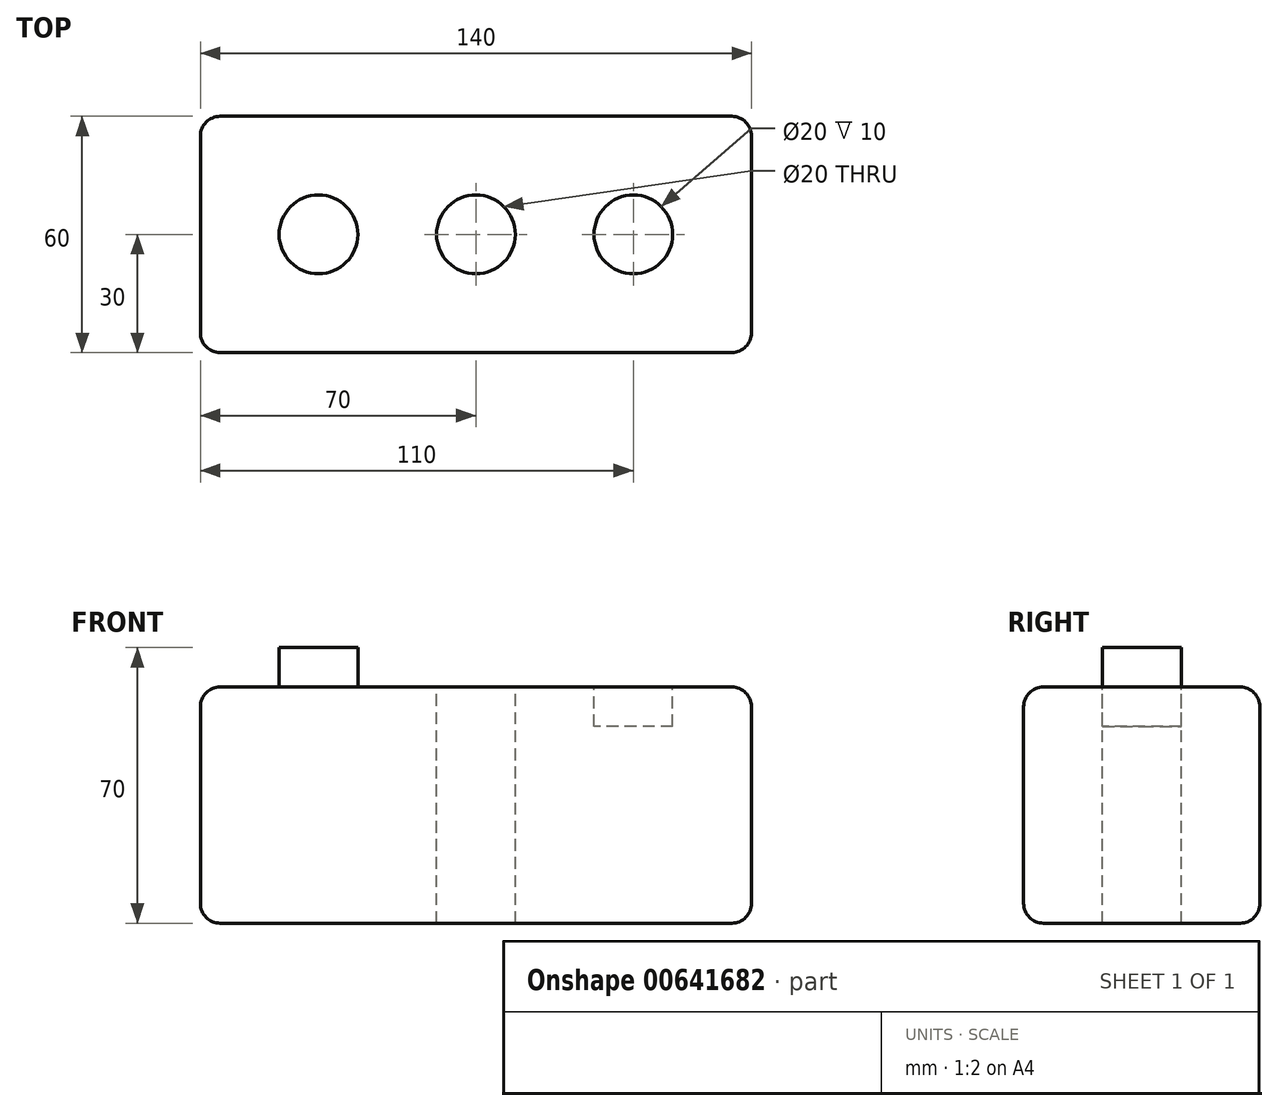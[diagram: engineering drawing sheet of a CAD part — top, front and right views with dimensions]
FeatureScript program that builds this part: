
annotation { "Feature Type Name" : "Feature", "Feature Type Description" : "" }
export const myFeature = defineFeature(function(context is Context, id is Id, definition is map)
    precondition{}
    {
        {
            var Q0;
            Q0=qCreatedBy(makeId("Top.planeOp"),FACE);
            var sketch = newSketch(context, id + "F0", { "sketchPlane" : qUnion([Q0])});
            skLineSegment(sketch, "E0.bottom", {"start": v(-70, 30) * mm, "end": v(70, 30) * mm});
            skLineSegment(sketch, "E0.top", {"start": v(-70, -30) * mm, "end": v(70, -30) * mm});
            skLineSegment(sketch, "E0.left", {"start": v(-70, 30) * mm, "end": v(-70, -30) * mm});
            skLineSegment(sketch, "E0.right", {"start": v(70, 30) * mm, "end": v(70, -30) * mm});
            skPoint(sketch, "E0.middle", {"position": v(0, 0) * mm});
            skSolve(sketch);
        }
        {
            var Q0;
            Q0 = qSketchRegion(id + "F0", true);
            extrude(context, id + "F1", {"entities" : qUnion([Q0]), "depth" : 60 * mm, "offsetDistance" : 25 * mm});
        }
        {
            var Q0;
            Q0=makeQuery(id+"F1.opExtrude","CAP_FACE",FACE,{"disambiguationData":[OSD([sQuery(id+"F0.wireOp",EDGE,"E0.bottom"),sQuery(id+"F0.wireOp",EDGE,"E0.top"),sQuery(id+"F0.wireOp",EDGE,"E0.left"),sQuery(id+"F0.wireOp",EDGE,"E0.right")])],"isStart":false});
            var sketch = newSketch(context, id + "F2", { "sketchPlane" : qUnion([Q0])});
            skCircle(sketch, "E1", {"center": v(-40, 0) * mm, "radius": 10 * mm});
            skSolve(sketch);
        }
        {
            var Q0;
            Q0=makeQuery(id+"F2.imprint","IMPRINT",FACE,{"disambiguationData":[TD([[makeQuery(id+"F2.imprint","IMPRINT",EDGE,{"derivedFrom":sQuery(id+"F2.wireOp",EDGE,"E1")}),-1.0]])]});
            var sketch = newSketch(context, id + "F3", { "sketchPlane" : qUnion([Q0])});
            skCircle(sketch, "E2", {"center": v(40, 0) * mm, "radius": 10 * mm});
            skSolve(sketch);
        }
        {
            var Q0;
            Q0=makeQuery(id+"F2.imprint","IMPRINT",FACE,{"disambiguationData":[TD([[makeQuery(id+"F2.imprint","IMPRINT",EDGE,{"derivedFrom":sQuery(id+"F2.wireOp",EDGE,"E1")}),-1.0]])]});
            var sketch = newSketch(context, id + "F4", { "sketchPlane" : qUnion([Q0])});
            skCircle(sketch, "E3", {"center": v(0, 0) * mm, "radius": 10 * mm});
            skSolve(sketch);
        }
        {
            var Q0;
            Q0 = qSketchRegion(id + "F2", true);
            extrude(context, id + "F5", {"entities" : qUnion([Q0]), "operationType" : NewBodyOperationType.ADD, "depth" : 10 * mm, "offsetDistance" : 25 * mm});
        }
        {
            var Q0;
            Q0 = qSketchRegion(id + "F3", true);
            extrude(context, id + "F6", {"entities" : qUnion([Q0]), "operationType" : NewBodyOperationType.REMOVE, "oppositeDirection" : true, "depth" : 10 * mm, "offsetDistance" : 25 * mm});
        }
        {
            var Q0;
            Q0 = qSketchRegion(id + "F4", true);
            extrude(context, id + "F7", {"entities" : qUnion([Q0]), "operationType" : NewBodyOperationType.REMOVE, "oppositeDirection" : true, "depth" : 95.7 * mm, "offsetDistance" : 25 * mm});
        }
        {
            var Q0;
            Q0=makeQuery(id+"F1.opExtrude","CAP_EDGE",EDGE,{"disambiguationData":[OSD([sQuery(id+"F0.wireOp",EDGE,"E0.left")])],"isStart":false});
            var Q1;
            Q1=makeQuery(id+"F1.opExtrude","CAP_EDGE",EDGE,{"disambiguationData":[OSD([sQuery(id+"F0.wireOp",EDGE,"E0.top")])],"isStart":false});
            var Q2;
            Q2=makeQuery(id+"F1.opExtrude","CAP_EDGE",EDGE,{"disambiguationData":[OSD([sQuery(id+"F0.wireOp",EDGE,"E0.bottom")])],"isStart":false});
            var Q3;
            Q3=makeQuery(id+"F1.opExtrude","CAP_EDGE",EDGE,{"disambiguationData":[OSD([sQuery(id+"F0.wireOp",EDGE,"E0.right")])],"isStart":false});
            var Q4;
            Q4=makeQuery(id+"F1.opExtrude","SWEPT_EDGE",EDGE,{"disambiguationData":[OSD([sQuery(id+"F0.wireOp",EDGE,"E0.top"),sQuery(id+"F0.wireOp",EDGE,"E0.left")])]});
            var Q5;
            Q5=makeQuery(id+"F1.opExtrude","SWEPT_EDGE",EDGE,{"disambiguationData":[OSD([sQuery(id+"F0.wireOp",EDGE,"E0.top"),sQuery(id+"F0.wireOp",EDGE,"E0.right")])]});
            var Q6;
            Q6=makeQuery(id+"F1.opExtrude","SWEPT_EDGE",EDGE,{"disambiguationData":[OSD([sQuery(id+"F0.wireOp",EDGE,"E0.bottom"),sQuery(id+"F0.wireOp",EDGE,"E0.left")])]});
            var Q7;
            Q7=makeQuery(id+"F1.opExtrude","SWEPT_EDGE",EDGE,{"disambiguationData":[OSD([sQuery(id+"F0.wireOp",EDGE,"E0.bottom"),sQuery(id+"F0.wireOp",EDGE,"E0.right")])]});
            var Q8;
            Q8=makeQuery(id+"F1.opExtrude","CAP_EDGE",EDGE,{"disambiguationData":[OSD([sQuery(id+"F0.wireOp",EDGE,"E0.bottom")])],"isStart":true});
            var Q9;
            Q9=makeQuery(id+"F1.opExtrude","CAP_EDGE",EDGE,{"disambiguationData":[OSD([sQuery(id+"F0.wireOp",EDGE,"E0.left")])],"isStart":true});
            var Q10;
            Q10=makeQuery(id+"F1.opExtrude","CAP_EDGE",EDGE,{"disambiguationData":[OSD([sQuery(id+"F0.wireOp",EDGE,"E0.top")])],"isStart":true});
            var Q11;
            Q11=makeQuery(id+"F1.opExtrude","CAP_EDGE",EDGE,{"disambiguationData":[OSD([sQuery(id+"F0.wireOp",EDGE,"E0.right")])],"isStart":true});
            fillet(context, id + "F8", {"entities" : qUnion([Q0, Q1, Q2, Q3, Q4, Q5, Q6, Q7, Q8, Q9, Q10, Q11]), "radius" : 5 * mm, "tangentPropagation" : true, "allowEdgeOverflow" : false});
        }
    });
